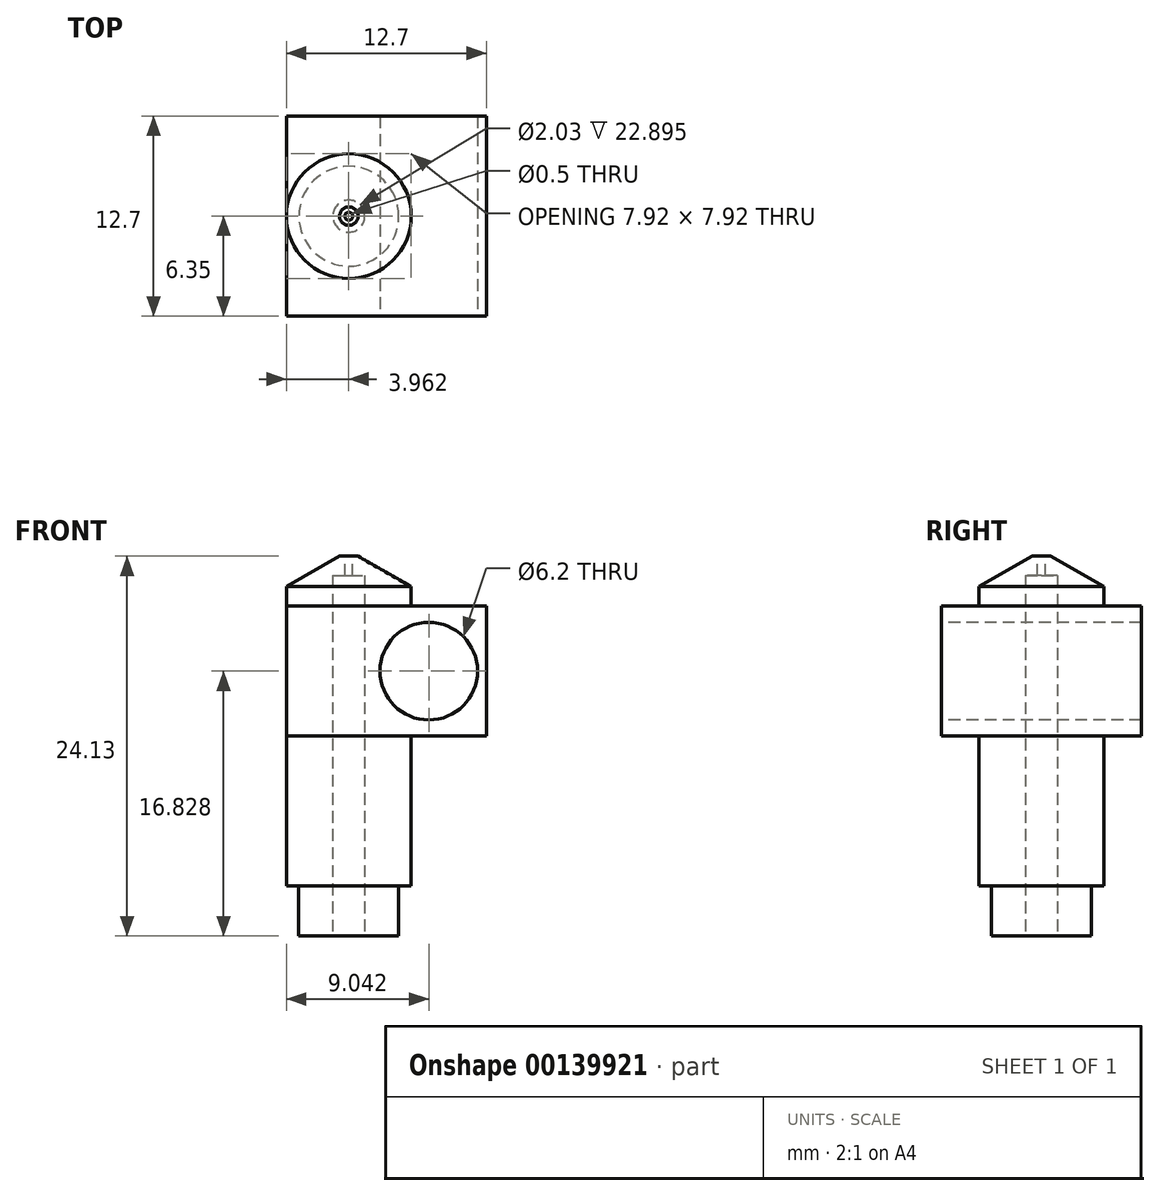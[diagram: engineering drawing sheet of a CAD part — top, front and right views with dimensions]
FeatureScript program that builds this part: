
annotation { "Feature Type Name" : "Feature", "Feature Type Description" : "" }
export const myFeature = defineFeature(function(context is Context, id is Id, definition is map)
    precondition{}
    {
        {
            var Q0;
            Q0=qCreatedBy(makeId("Top.planeOp"),FACE);
            var sketch = newSketch(context, id + "F0", { "sketchPlane" : qUnion([Q0])});
            skLineSegment(sketch, "E0.bottom", {"start": v(-6.35, 6.35) * mm, "end": v(6.35, 6.35) * mm});
            skLineSegment(sketch, "E0.top", {"start": v(-6.35, -6.35) * mm, "end": v(6.35, -6.35) * mm});
            skLineSegment(sketch, "E0.left", {"start": v(-6.35, 6.35) * mm, "end": v(-6.35, -6.35) * mm});
            skLineSegment(sketch, "E0.right", {"start": v(6.35, 6.35) * mm, "end": v(6.35, -6.35) * mm});
            skLineSegment(sketch, "E1", {"start": v(-6.35, 6.35) * mm, "end": v(6.35, -6.35) * mm, "construction": true});
            skSolve(sketch);
        }
        {
            var Q0;
            Q0=makeQuery(id+"F0.imprint","IMPRINT",FACE,{"disambiguationData":[TD([[makeQuery(id+"F0.imprint","IMPRINT",EDGE,{"derivedFrom":sQuery(id+"F0.wireOp",EDGE,"E0.bottom")}),-1.0]])]});
            extrude(context, id + "F1", {"entities" : qUnion([Q0]), "depth" : 8.25 * mm});
        }
        {
            var Q0;
            Q0=makeQuery(id+"F1.opExtrude","SWEPT_FACE",FACE,{"disambiguationData":[OSD([sQuery(id+"F0.wireOp",EDGE,"E0.top")])]});
            var sketch = newSketch(context, id + "F2", { "sketchPlane" : qUnion([Q0])});
            skCircle(sketch, "E2", {"center": v(2.7, 4.13) * mm, "radius": 3.1 * mm});
            skLineSegment(sketch, "E3", {"start": v(-6.35, 4.13) * mm, "end": v(6.35, 4.13) * mm, "construction": true});
            skPoint(sketch, "E4", {"position": v(5.8, 4.13) * mm});
            skSolve(sketch);
        }
        {
            var Q0;
            Q0=makeQuery(id+"F2.imprint","IMPRINT",FACE,{"disambiguationData":[TD([[makeQuery(id+"F2.imprint","IMPRINT",EDGE,{"derivedFrom":sQuery(id+"F2.wireOp",EDGE,"E2")}),1.0]])]});
            extrude(context, id + "F3", {"entities" : qUnion([Q0]), "operationType" : NewBodyOperationType.REMOVE, "endBound" : BoundingType.THROUGH_ALL, "oppositeDirection" : true, "depth" : 25.4 * mm});
        }
        {
            var Q0;
            Q0=qCreatedBy(makeId("Front.planeOp"),FACE);
            var sketch = newSketch(context, id + "F4", { "sketchPlane" : qUnion([Q0])});
            skLineSegment(sketch, "E5", {"start": v(-2.39, 18.71) * mm, "end": v(-2.39, -12.7) * mm});
            skLineSegment(sketch, "E6.0", {"start": v(-6.35, 8.26) * mm, "end": v(6.35, 8.26) * mm, "construction": true});
            skLineSegment(sketch, "E6.1", {"start": v(-6.35, 8.26) * mm, "end": v(-6.35, 0) * mm, "construction": true});
            skLineSegment(sketch, "E7", {"start": v(-6.35, 8.26) * mm, "end": v(-6.35, 9.5) * mm});
            skLineSegment(sketch, "E8", {"start": v(-6.35, 9.5) * mm, "end": v(-2.97, 11.43) * mm});
            skLineSegment(sketch, "E9", {"start": v(-2.97, 11.43) * mm, "end": v(-2.39, 11.43) * mm});
            skLineSegment(sketch, "E10", {"start": v(-6.35, 0) * mm, "end": v(-6.35, -9.53) * mm});
            skLineSegment(sketch, "E11", {"start": v(-6.35, -9.53) * mm, "end": v(-5.56, -9.53) * mm});
            skLineSegment(sketch, "E12", {"start": v(-5.56, -9.53) * mm, "end": v(-5.56, -12.7) * mm});
            skLineSegment(sketch, "E13", {"start": v(-5.56, -12.7) * mm, "end": v(-2.39, -12.7) * mm});
            skLineSegment(sketch, "E14", {"start": v(-6.35, 0) * mm, "end": v(-2.39, 0) * mm});
            skLineSegment(sketch, "E15", {"start": v(-6.35, 8.26) * mm, "end": v(-2.39, 8.26) * mm});
            skCircle(sketch, "E16", {"center": v(-6.84, 9.34) * mm, "radius": 0.1 * mm});
            skLineSegment(sketch, "E17", {"start": v(-7.28, 9.24) * mm, "end": v(-6.84, 9.24) * mm});
            skLineSegment(sketch, "E18", {"start": v(-6.74, 9.34) * mm, "end": v(-6.74, 12.03) * mm});
            skCircle(sketch, "E19", {"center": v(-3, 11.53) * mm, "radius": 0.1 * mm});
            skLineSegment(sketch, "E20", {"start": v(-2.97, 11.43) * mm, "end": v(-3.5, 11.43) * mm});
            skLineSegment(sketch, "E21", {"start": v(-2.9, 11.53) * mm, "end": v(-2.9, 11.9) * mm});
            skSolve(sketch);
        }
        {
            var Q0;
            Q0=makeQuery(id+"F4.imprint","IMPRINT",FACE,{"disambiguationData":[TD([[makeQuery(id+"F4.imprint","IMPRINT",EDGE,{"derivedFrom":sQuery(id+"F4.wireOp",EDGE,"E7")}),-1.0]])]});
            var Q1;
            Q1=sQuery(id+"F4.wireOp",EDGE,"E5");
            revolve(context, id + "F5", {"operationType" : NewBodyOperationType.ADD, "entities" : qUnion([Q0]), "axis" : qUnion([Q1]), "revolveType" : RevolveType.FULL});
        }
        {
            var Q0;
            Q0=makeQuery(id+"F4.imprint","IMPRINT",FACE,{"disambiguationData":[TD([[makeQuery(id+"F4.imprint","IMPRINT",EDGE,{"derivedFrom":sQuery(id+"F4.wireOp",EDGE,"E10")}),1.0]])]});
            var Q1;
            Q1=sQuery(id+"F4.wireOp",EDGE,"E5");
            revolve(context, id + "F6", {"operationType" : NewBodyOperationType.ADD, "entities" : qUnion([Q0]), "axis" : qUnion([Q1]), "revolveType" : RevolveType.FULL});
        }
        {
            var Q0;
            Q0=makeQuery(id+"F6.opRevolve","SWEPT_FACE",FACE,{"disambiguationData":[OSD([sQuery(id+"F4.wireOp",EDGE,"E13")])]});
            var sketch = newSketch(context, id + "F7", { "sketchPlane" : qUnion([Q0])});
            skCircle(sketch, "E22", {"center": v(-2.39, 0) * mm, "radius": 1.02 * mm});
            skSolve(sketch);
        }
        {
            var Q0;
            Q0=makeQuery(id+"F7.imprint","IMPRINT",FACE,{"disambiguationData":[TD([[makeQuery(id+"F7.imprint","IMPRINT",EDGE,{"derivedFrom":sQuery(id+"F7.wireOp",EDGE,"E22")}),1.0]])]});
            extrude(context, id + "F8", {"entities" : qUnion([Q0]), "operationType" : NewBodyOperationType.REMOVE, "oppositeDirection" : true, "depth" : 22.9 * mm});
        }
        {
            var Q0;
            Q0=makeQuery(id+"F5.opRevolve","SWEPT_FACE",FACE,{"disambiguationData":[OSD([sQuery(id+"F4.wireOp",EDGE,"E9")])]});
            var sketch = newSketch(context, id + "F9", { "sketchPlane" : qUnion([Q0])});
            skCircle(sketch, "E23", {"center": v(-2.39, 0) * mm, "radius": 0.25 * mm});
            skSolve(sketch);
        }
        {
            var Q0;
            Q0=makeQuery(id+"F9.imprint","IMPRINT",FACE,{"disambiguationData":[TD([[makeQuery(id+"F9.imprint","IMPRINT",EDGE,{"derivedFrom":sQuery(id+"F9.wireOp",EDGE,"E23")}),1.0]])]});
            extrude(context, id + "F10", {"entities" : qUnion([Q0]), "operationType" : NewBodyOperationType.REMOVE, "endBound" : BoundingType.THROUGH_ALL, "oppositeDirection" : true, "depth" : 25.4 * mm});
        }
    });
